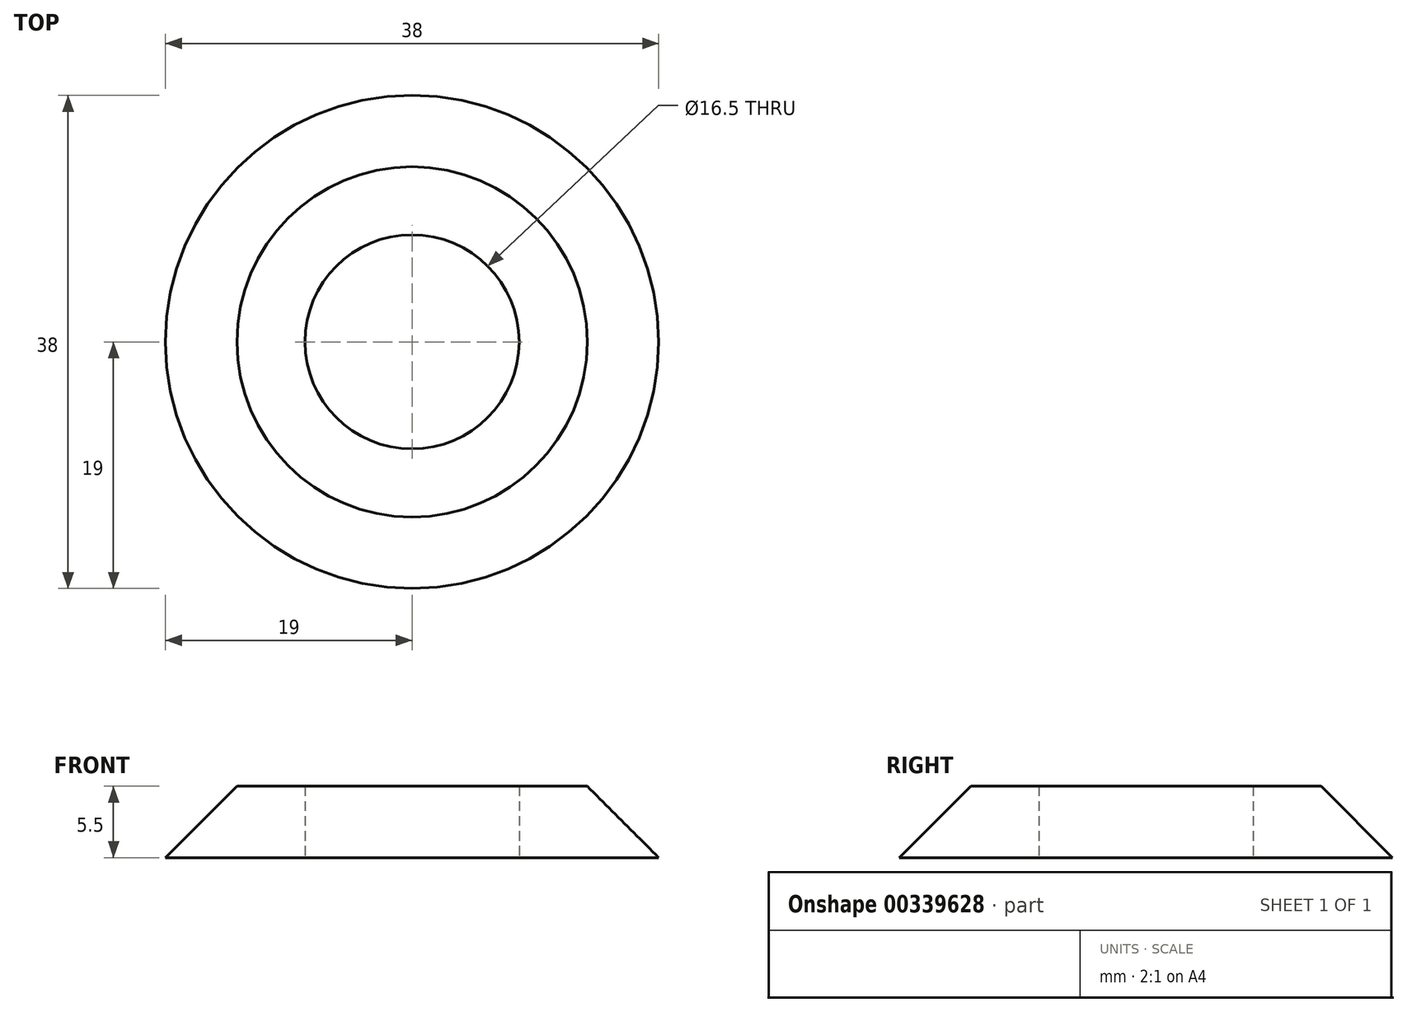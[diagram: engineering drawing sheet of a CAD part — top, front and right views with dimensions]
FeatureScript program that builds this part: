
annotation { "Feature Type Name" : "Feature", "Feature Type Description" : "" }
export const myFeature = defineFeature(function(context is Context, id is Id, definition is map)
    precondition{}
    {
        {
            var Q0;
            Q0=qCreatedBy(makeId("Top.planeOp"),FACE);
            var sketch = newSketch(context, id + "F0", { "sketchPlane" : qUnion([Q0])});
            skCircle(sketch, "E0", {"center": v(0, 0) * mm, "radius": 8.25 * mm});
            skCircle(sketch, "E1", {"center": v(0, 0) * mm, "radius": 19 * mm});
            skSolve(sketch);
        }
        {
            var Q0;
            Q0=makeQuery(id+"F0.imprint","IMPRINT",FACE,{"disambiguationData":[TD([[makeQuery(id+"F0.imprint","IMPRINT",EDGE,{"derivedFrom":sQuery(id+"F0.wireOp",EDGE,"E0")}),-1.0]])]});
            extrude(context, id + "F1", {"entities" : qUnion([Q0]), "depth" : 5.5 * mm});
        }
        {
            var Q0;
            Q0=makeQuery(id+"F1.opExtrude","CAP_EDGE",EDGE,{"disambiguationData":[OSD([sQuery(id+"F0.wireOp",EDGE,"E1")])],"isStart":false});
            chamfer(context, id + "F2", {"entities" : qUnion([Q0]), "width" : (5.5) * mm, "tangentPropagation" : true});
        }
    });
